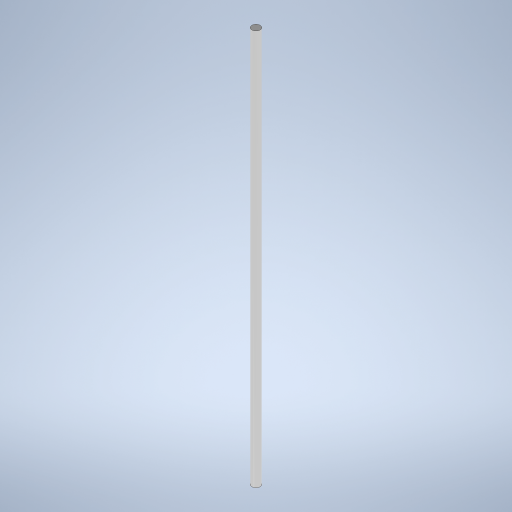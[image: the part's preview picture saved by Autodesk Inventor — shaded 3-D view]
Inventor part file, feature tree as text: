
AUTODESK INVENTOR PART (.ipt)
format: ipt  version: 2024 (Build 280153000, 153)  size: 230,400 bytes
history: native  units: in
note: dims shown in document units (in); Inventor stores cm internally (conversion verified against a paired STEP export)
features: extrude x1, sketch x1
ambient origin geometry x8: Origin, YZ Plane, XZ Plane, XY Plane, X Axis, Y Axis, Z Axis, Center Point
bodies: Solid1 (feature_tree)
feature tree (2):
  extrude  "Extrusion1"  Depth=17.0in TaperAngle=0.0deg
  sketch  "Sketch1"  dims[d0=0.3543in d1=17.0in d2=0.0in]
